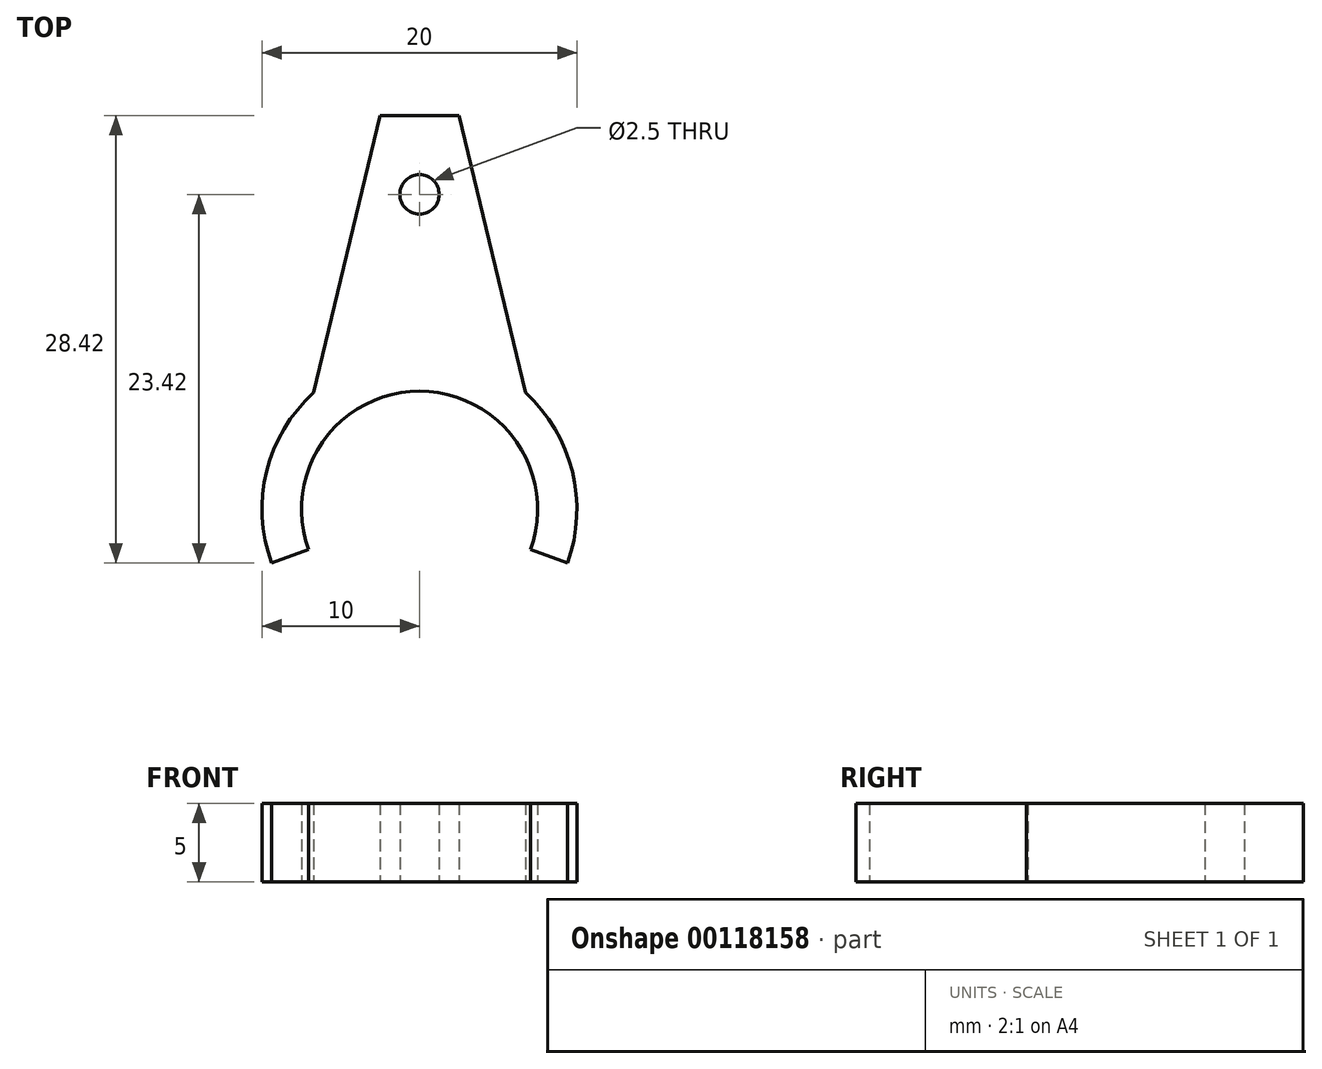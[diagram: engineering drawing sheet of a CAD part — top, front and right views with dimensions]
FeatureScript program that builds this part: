
annotation { "Feature Type Name" : "Feature", "Feature Type Description" : "" }
export const myFeature = defineFeature(function(context is Context, id is Id, definition is map)
    precondition{}
    {
        {
            var Q0;
            Q0=qCreatedBy(makeId("Top.planeOp"),FACE);
            var sketch = newSketch(context, id + "F0", { "sketchPlane" : qUnion([Q0])});
            skCircle(sketch, "E0", {"center": v(0, 0) * mm, "radius": 10 * mm});
            skSolve(sketch);
        }
        {
            var Q0;
            Q0 = qSketchRegion(id + "F0", true);
            extrude(context, id + "F1", {"entities" : qUnion([Q0]), "depth" : 5 * mm});
        }
        {
            var Q0;
            Q0=qCreatedBy(makeId("Top.planeOp"),FACE);
            var sketch = newSketch(context, id + "F2", { "sketchPlane" : qUnion([Q0])});
            skLineSegment(sketch, "E1.bottom", {"start": v(-8.5, 0) * mm, "end": v(8.5, 0) * mm});
            skLineSegment(sketch, "E1.top", {"start": v(-2.5, 25) * mm, "end": v(2.5, 25) * mm});
            skLineSegment(sketch, "E1.left", {"start": v(-8.5, 0) * mm, "end": v(-2.5, 25) * mm});
            skLineSegment(sketch, "E1.right", {"start": v(8.5, 0) * mm, "end": v(2.5, 25) * mm});
            skLineSegment(sketch, "E2", {"start": v(0, 0) * mm, "end": v(2.5, 25) * mm, "construction": true});
            skLineSegment(sketch, "E3", {"start": v(0, 0) * mm, "end": v(-2.5, 25) * mm, "construction": true});
            skSolve(sketch);
        }
        {
            var Q0;
            Q0 = qSketchRegion(id + "F2", true);
            extrude(context, id + "F3", {"entities" : qUnion([Q0]), "operationType" : NewBodyOperationType.ADD, "depth" : 5 * mm});
        }
        {
            var Q0;
            Q0=qCreatedBy(makeId("Top.planeOp"),FACE);
            var sketch = newSketch(context, id + "F4", { "sketchPlane" : qUnion([Q0])});
            skCircle(sketch, "E4", {"center": v(0, 0) * mm, "radius": 7.5 * mm});
            skSolve(sketch);
        }
        {
            var Q0;
            Q0 = qSketchRegion(id + "F4", true);
            extrude(context, id + "F5", {"entities" : qUnion([Q0]), "operationType" : NewBodyOperationType.REMOVE, "depth" : 5 * mm});
        }
        {
            var Q0;
            Q0=qCreatedBy(makeId("Top.planeOp"),FACE);
            var sketch = newSketch(context, id + "F6", { "sketchPlane" : qUnion([Q0])});
            skLineSegment(sketch, "E5", {"start": v(0, 0) * mm, "end": v(-19.8, -7.2) * mm});
            skLineSegment(sketch, "E6", {"start": v(-19.8, -7.2) * mm, "end": v(0, -14.42) * mm});
            skLineSegment(sketch, "E7", {"start": v(0, -14.42) * mm, "end": v(19.8, -7.2) * mm});
            skLineSegment(sketch, "E8", {"start": v(19.8, -7.2) * mm, "end": v(0, 0) * mm});
            skLineSegment(sketch, "E9", {"start": v(-19.8, -7.2) * mm, "end": v(19.8, -7.2) * mm, "construction": true});
            skSolve(sketch);
        }
        {
            var Q0;
            Q0=makeQuery(id+"F6.imprint","IMPRINT",FACE,{"disambiguationData":[TD([[makeQuery(id+"F6.imprint","IMPRINT",EDGE,{"derivedFrom":sQuery(id+"F6.wireOp",EDGE,"E5")}),1.0]])]});
            extrude(context, id + "F7", {"entities" : qUnion([Q0]), "operationType" : NewBodyOperationType.REMOVE, "depth" : 5 * mm});
        }
        {
            var Q0;
            Q0=qCreatedBy(makeId("Top.planeOp"),FACE);
            var sketch = newSketch(context, id + "F8", { "sketchPlane" : qUnion([Q0])});
            skCircle(sketch, "E10", {"center": v(0, 20) * mm, "radius": 1.25 * mm});
            skSolve(sketch);
        }
        {
            var Q0;
            Q0 = qSketchRegion(id + "F8", true);
            extrude(context, id + "F9", {"entities" : qUnion([Q0]), "operationType" : NewBodyOperationType.REMOVE, "depth" : 5 * mm});
        }
    });
